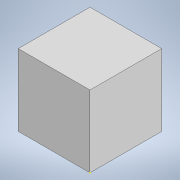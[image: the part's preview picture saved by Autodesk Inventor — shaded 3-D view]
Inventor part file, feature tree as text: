
AUTODESK INVENTOR PART (.ipt)
format: ipt  version: 2021 (Build 250183000, 183)  size: 108,032 bytes
history: native  units: in
note: dims shown in document units (in); Inventor stores cm internally (conversion verified against a paired STEP export)
features: sketch x3, extrude x2, chamfer x1, projected_geometry x1
ambient origin geometry x8: Origin, YZ Plane, XZ Plane, XY Plane, X Axis, Y Axis, Z Axis, Center Point
bodies: Solid1 (feature_tree)
feature tree (7):
  sketch  "Sketch1"  dims[d1=0.6299in d2=0.6299in]
  extrude  "Extrusion1"  Depth=0.6299in
  extrude  "Extrusion3"  Depth=0.6299in
  chamfer  "Chamfer1"  Distance=0.2598in
  sketch  "Sketch2"  dims[d8=0.6299in d9=0.0in d28=0.1299in]
  sketch  "Sketch4"  dims[d29=0.2559in d30=0.2598in d31=0.5118in d32=0.2598in d33=0.0in d34=0.1299in d35=0.0787in d36=45.0deg]
  projected_geometry  "Projected Loop1"
